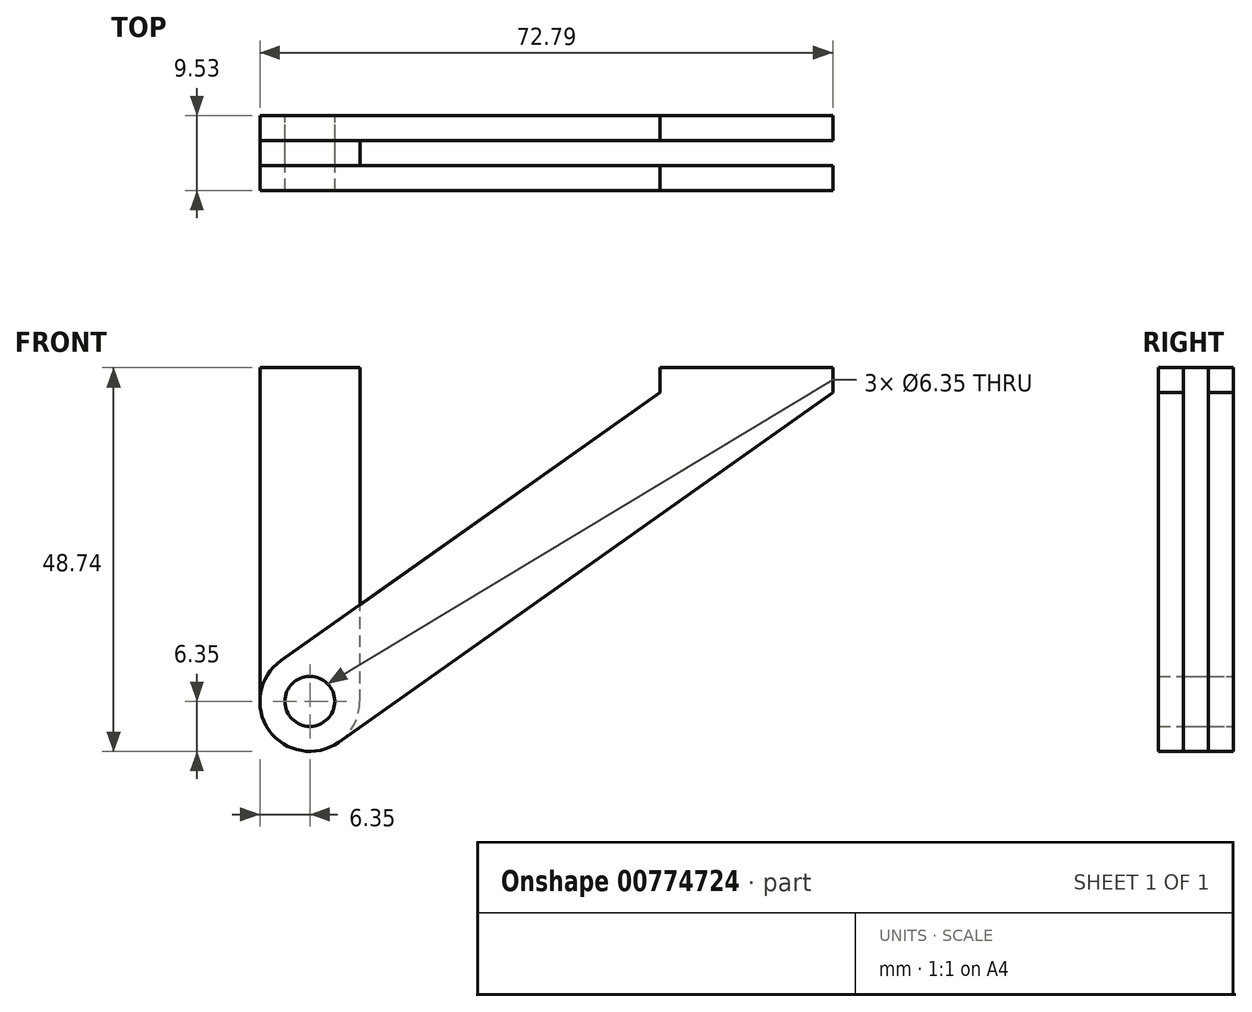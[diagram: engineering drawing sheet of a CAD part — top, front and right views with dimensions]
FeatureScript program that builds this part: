
annotation { "Feature Type Name" : "Feature", "Feature Type Description" : "" }
export const myFeature = defineFeature(function(context is Context, id is Id, definition is map)
    precondition{}
    {
        {
            var Q0;
            Q0=qCreatedBy(makeId("Front.planeOp"),FACE);
            var sketch = newSketch(context, id + "F0", { "sketchPlane" : qUnion([Q0])});
            skLineSegment(sketch, "E0.bottom", {"start": v(0, 0) * mm, "end": v(12.7, 0) * mm});
            skLineSegment(sketch, "E0.top", {"start": v(0, 48.74) * mm, "end": v(12.7, 48.74) * mm});
            skLineSegment(sketch, "E0.left", {"start": v(0, 0) * mm, "end": v(0, 48.74) * mm});
            skLineSegment(sketch, "E0.right", {"start": v(12.7, 0) * mm, "end": v(12.7, 48.74) * mm});
            skLineSegment(sketch, "E1", {"start": v(6.35, 0) * mm, "end": v(6.35, 6.35) * mm});
            skCircle(sketch, "E2", {"center": v(6.35, 6.35) * mm, "radius": 3.18 * mm});
            skSolve(sketch);
        }
        {
            var Q0;
            Q0=makeQuery(id+"F0.imprint","IMPRINT",FACE,{"disambiguationData":[TD([[makeQuery(id+"F0.imprint","IMPRINT",EDGE,{"derivedFrom":sQuery(id+"F0.wireOp",EDGE,"E0.bottom")}),1.0]])]});
            extrude(context, id + "F1", {"entities" : qUnion([Q0]), "depth" : 3.17 * mm, "offsetDistance" : 25.4 * mm});
        }
        {
            var Q0;
            Q0=makeQuery(id+"F1.opExtrude","SWEPT_EDGE",EDGE,{"disambiguationData":[OSD([sQuery(id+"F0.wireOp",EDGE,"E0.bottom"),sQuery(id+"F0.wireOp",EDGE,"E0.right")])]});
            var Q1;
            Q1=makeQuery(id+"F1.opExtrude","SWEPT_EDGE",EDGE,{"disambiguationData":[OSD([sQuery(id+"F0.wireOp",EDGE,"E0.bottom"),sQuery(id+"F0.wireOp",EDGE,"E0.left")])]});
            fillet(context, id + "F2", {"entities" : qUnion([Q0, Q1]), "radius" : 6.35 * mm, "tangentPropagation" : true, "allowEdgeOverflow" : false});
        }
        {
            var Q0;
            Q0=qCreatedBy(makeId("Front.planeOp"),FACE);
            cPlane(context, id + "F3", {"entities" : qUnion([Q0]), "cplaneType" : CPlaneType.OFFSET, "offset" : 3.17 * mm, "width" : 152.4 * mm, "height" : 152.4 * mm});
        }
        {
            var Q0;
            Q0=qCreatedBy(id+"F3.planeOp",FACE);
            var sketch = newSketch(context, id + "F4", { "sketchPlane" : qUnion([Q0])});
            skCircle(sketch, "E3.0", {"center": v(6.35, 6.35) * mm, "radius": 3.18 * mm});
            skCircle(sketch, "E4", {"center": v(6.35, 6.35) * mm, "radius": 6.35 * mm});
            skLineSegment(sketch, "E5.0", {"start": v(0, 48.74) * mm, "end": v(12.7, 48.74) * mm});
            skLineSegment(sketch, "E6", {"start": v(12.7, 48.74) * mm, "end": v(50.8, 48.74) * mm});
            skLineSegment(sketch, "E7", {"start": v(50.8, 48.74) * mm, "end": v(50.8, 45.57) * mm});
            skLineSegment(sketch, "E8", {"start": v(63.5, 45.57) * mm, "end": v(50.8, 45.57) * mm});
            skLineSegment(sketch, "E9", {"start": v(50.8, 45.57) * mm, "end": v(2.68, 11.53) * mm});
            skLineSegment(sketch, "E10", {"start": v(2.68, 11.53) * mm, "end": v(10.02, 1.17) * mm});
            skLineSegment(sketch, "E11", {"start": v(50.8, 45.57) * mm, "end": v(72.8, 45.57) * mm});
            skLineSegment(sketch, "E12", {"start": v(10.02, 1.17) * mm, "end": v(72.8, 45.57) * mm});
            skLineSegment(sketch, "E13", {"start": v(72.8, 45.57) * mm, "end": v(72.8, 48.74) * mm});
            skLineSegment(sketch, "E14", {"start": v(50.8, 48.74) * mm, "end": v(72.8, 48.74) * mm});
            skSolve(sketch);
        }
        {
            var Q0;
            {var subQ0=sQuery(id+"F4.wireOp",EDGE,"E10");var subQ1=sQuery(id+"F4.wireOp",EDGE,"E3.0");var subQ2=makeQuery(id+"F4.imprint","INTERSECT",VERTEX,{"disambiguationData":[OD(0.0)],"derivedFrom":[subQ1,subQ0]});Q0=makeQuery(id+"F4.imprint","IMPRINT",FACE,{"disambiguationData":[TD([[makeQuery(id+"F4.imprint","IMPRINT",EDGE,{"disambiguationData":[TD([[subQ2,-1.0]])],"derivedFrom":subQ1}),-1.0]])]});}
            var Q1;
            {var subQ0=sQuery(id+"F4.wireOp",EDGE,"E10");var subQ1=sQuery(id+"F4.wireOp",EDGE,"E3.0");var subQ2=makeQuery(id+"F4.imprint","INTERSECT",VERTEX,{"disambiguationData":[OD(0.0)],"derivedFrom":[subQ1,subQ0]});Q1=makeQuery(id+"F4.imprint","IMPRINT",FACE,{"disambiguationData":[TD([[makeQuery(id+"F4.imprint","IMPRINT",EDGE,{"disambiguationData":[TD([[subQ2,1.0]])],"derivedFrom":subQ1}),-1.0]])]});}
            var Q2;
            {var subQ1=sQuery(id+"F4.wireOp",EDGE,"E9");Q2=makeQuery(id+"F4.imprint","IMPRINT",FACE,{"disambiguationData":[TD([[makeQuery(id+"F4.imprint","IMPRINT",EDGE,{"derivedFrom":subQ1}),1.0]])]});}
            var Q3;
            {var subQ3=sQuery(id+"F4.wireOp",EDGE,"E7");Q3=makeQuery(id+"F4.imprint","IMPRINT",FACE,{"disambiguationData":[TD([[makeQuery(id+"F4.imprint","IMPRINT",EDGE,{"derivedFrom":subQ3}),1.0]])]});}
            extrude(context, id + "F5", {"entities" : qUnion([Q0, Q1, Q2, Q3]), "depth" : 3.17 * mm, "offsetDistance" : 25.4 * mm});
        }
        {
            var Q0;
            Q0=makeQuery(id+"F5.opExtrude","SWEPT_BODY",BODY,{"disambiguationData":[OSD([sQuery(id+"F4.wireOp",EDGE,"E3.0"),sQuery(id+"F4.wireOp",EDGE,"E4"),sQuery(id+"F4.wireOp",EDGE,"E7"),sQuery(id+"F4.wireOp",EDGE,"E9"),sQuery(id+"F4.wireOp",EDGE,"E12"),sQuery(id+"F4.wireOp",EDGE,"E13"),sQuery(id+"F4.wireOp",EDGE,"E14")])]});
            transform(context, id + "F6", {"entities" : qUnion([Q0]), "transformType" : TransformType.TRANSLATION_3D, "dx" : 0 * mm, "dy" : 6.35 * mm, "dz" : 0 * mm, "makeCopy" : true});
        }
        {
            var Q0;
            Q0=makeQuery(id+"F6.opPattern","COPY",FACE,{"derivedFrom":makeQuery(id+"F5.opExtrude","CAP_FACE",FACE,{"disambiguationData":[OSD([sQuery(id+"F4.wireOp",EDGE,"E3.0"),sQuery(id+"F4.wireOp",EDGE,"E4"),sQuery(id+"F4.wireOp",EDGE,"E7"),sQuery(id+"F4.wireOp",EDGE,"E9"),sQuery(id+"F4.wireOp",EDGE,"E12"),sQuery(id+"F4.wireOp",EDGE,"E13"),sQuery(id+"F4.wireOp",EDGE,"E14")])],"isStart":true}),"instanceName":"1"});
            var sketch = newSketch(context, id + "F7", { "sketchPlane" : qUnion([Q0])});
            skCircle(sketch, "E15.0", {"center": v(-6.35, 6.35) * mm, "radius": 3.18 * mm});
            skSolve(sketch);
        }
        {
            var Q0;
            Q0=makeQuery(id+"F7.imprint","IMPRINT",FACE,{"disambiguationData":[TD([[makeQuery(id+"F7.imprint","IMPRINT",EDGE,{"derivedFrom":sQuery(id+"F7.wireOp",EDGE,"E15.0")}),-1.0]])]});
            extrude(context, id + "F8", {"entities" : qUnion([Q0]), "oppositeDirection" : true, "depth" : 9.52 * mm, "offsetDistance" : 25.4 * mm});
        }
    });
